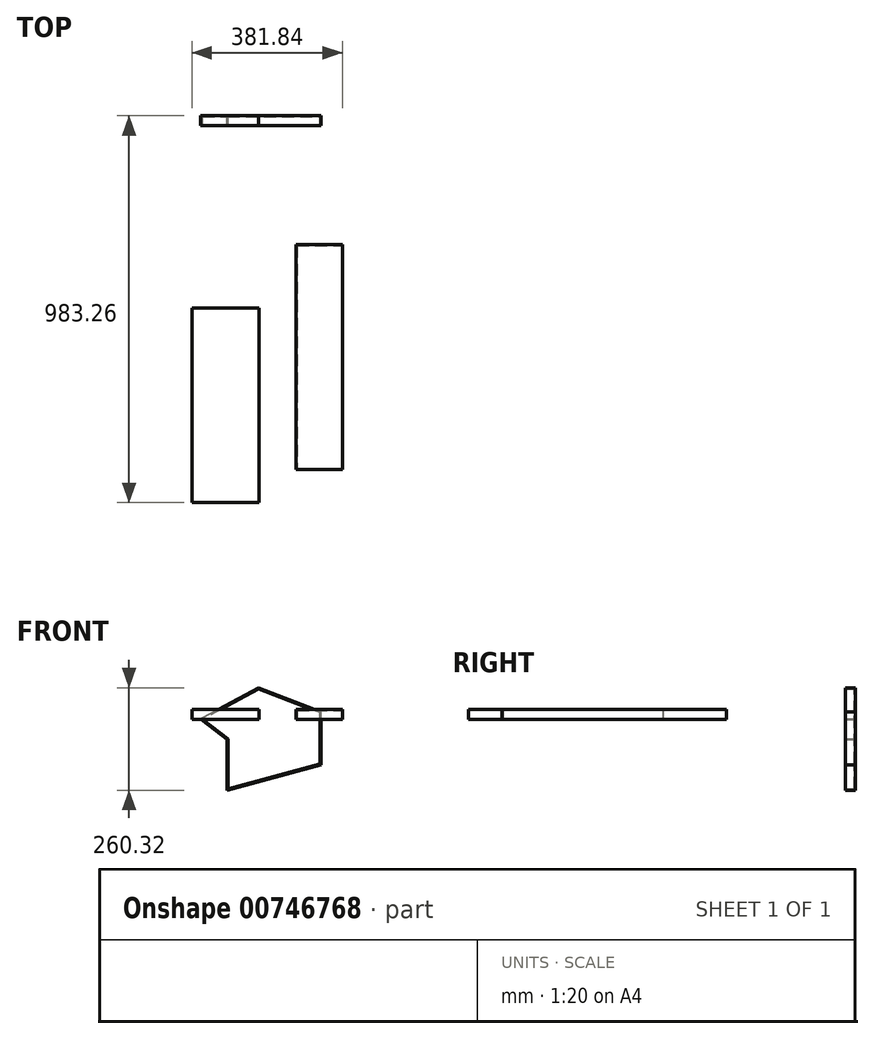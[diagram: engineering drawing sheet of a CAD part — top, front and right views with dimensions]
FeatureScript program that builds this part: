
annotation { "Feature Type Name" : "Feature", "Feature Type Description" : "" }
export const myFeature = defineFeature(function(context is Context, id is Id, definition is map)
    precondition{}
    {
        {
            var Q0;
            Q0=qCreatedBy(makeId("Front.planeOp"),FACE);
            var sketch = newSketch(context, id + "F0", { "sketchPlane" : qUnion([Q0])});
            skLineSegment(sketch, "E0", {"start": v(-238.43, -50.81) * mm, "end": v(-238.43, -180.2) * mm});
            skLineSegment(sketch, "E1", {"start": v(-238.43, -180.2) * mm, "end": v(0, -115.4) * mm});
            skLineSegment(sketch, "E2", {"start": v(0, -115.4) * mm, "end": v(0, 18.6) * mm});
            skLineSegment(sketch, "E3", {"start": v(-238.43, -50.81) * mm, "end": v(0, 18.6) * mm});
            skLineSegment(sketch, "E4", {"start": v(0, 18.6) * mm, "end": v(-158.1, 80.13) * mm});
            skLineSegment(sketch, "E5", {"start": v(-158.1, 80.13) * mm, "end": v(-305.4, 0) * mm});
            skLineSegment(sketch, "E6", {"start": v(-305.4, 0.58) * mm, "end": v(-238.43, -50.81) * mm});
            skSolve(sketch);
        }
        {
            var Q0;
            Q0 = qSketchRegion(id + "F0", true);
            extrude(context, id + "F1", {"entities" : qUnion([Q0]), "depth" : 25 * mm, "offsetDistance" : 25 * mm});
        }
        {
            var Q0;
            Q0=qCreatedBy(makeId("Top.planeOp"),FACE);
            var sketch = newSketch(context, id + "F2", { "sketchPlane" : qUnion([Q0])});
            skLineSegment(sketch, "E7.bottom", {"start": v(-62.6, -327.91) * mm, "end": v(54.86, -327.91) * mm});
            skLineSegment(sketch, "E7.top", {"start": v(-62.6, -898.3) * mm, "end": v(54.86, -898.3) * mm});
            skLineSegment(sketch, "E7.left", {"start": v(-62.6, -327.91) * mm, "end": v(-62.6, -898.3) * mm});
            skLineSegment(sketch, "E7.right", {"start": v(54.86, -327.91) * mm, "end": v(54.86, -898.3) * mm});
            skLineSegment(sketch, "E8.bottom", {"start": v(-326.98, -489.2) * mm, "end": v(-157.12, -489.2) * mm});
            skLineSegment(sketch, "E8.top", {"start": v(-326.98, -983.26) * mm, "end": v(-157.12, -983.26) * mm});
            skLineSegment(sketch, "E8.left", {"start": v(-326.98, -489.2) * mm, "end": v(-326.98, -983.26) * mm});
            skLineSegment(sketch, "E8.right", {"start": v(-157.12, -489.2) * mm, "end": v(-157.12, -983.26) * mm});
            skSolve(sketch);
        }
        {
            var Q0;
            Q0 = qSketchRegion(id + "F2", true);
            extrude(context, id + "F3", {"entities" : qUnion([Q0]), "depth" : 25 * mm, "offsetDistance" : 25 * mm});
        }
        {
            var Q0;
            Q0=makeQuery(id+"F3.opExtrude","CAP_FACE",FACE,{"disambiguationData":[OSD([sQuery(id+"F2.wireOp",EDGE,"E7.bottom"),sQuery(id+"F2.wireOp",EDGE,"E7.top"),sQuery(id+"F2.wireOp",EDGE,"E7.left"),sQuery(id+"F2.wireOp",EDGE,"E7.right")])],"isStart":true});
            shell(context, id + "F4", {"entities" : qUnion([Q0]), "thickness" : 2.5 * mm});
        }
        {
            var Q0;
            Q0=makeQuery(id+"F1.opExtrude","CAP_FACE",FACE,{"disambiguationData":[OSD([sQuery(id+"F0.wireOp",EDGE,"E0"),sQuery(id+"F0.wireOp",EDGE,"E1"),sQuery(id+"F0.wireOp",EDGE,"E2"),sQuery(id+"F0.wireOp",EDGE,"E4"),sQuery(id+"F0.wireOp",EDGE,"E5"),sQuery(id+"F0.wireOp",EDGE,"E6")])],"isStart":false});
            shell(context, id + "F5", {"entities" : qUnion([Q0]), "thickness" : 2.5 * mm});
        }
    });
